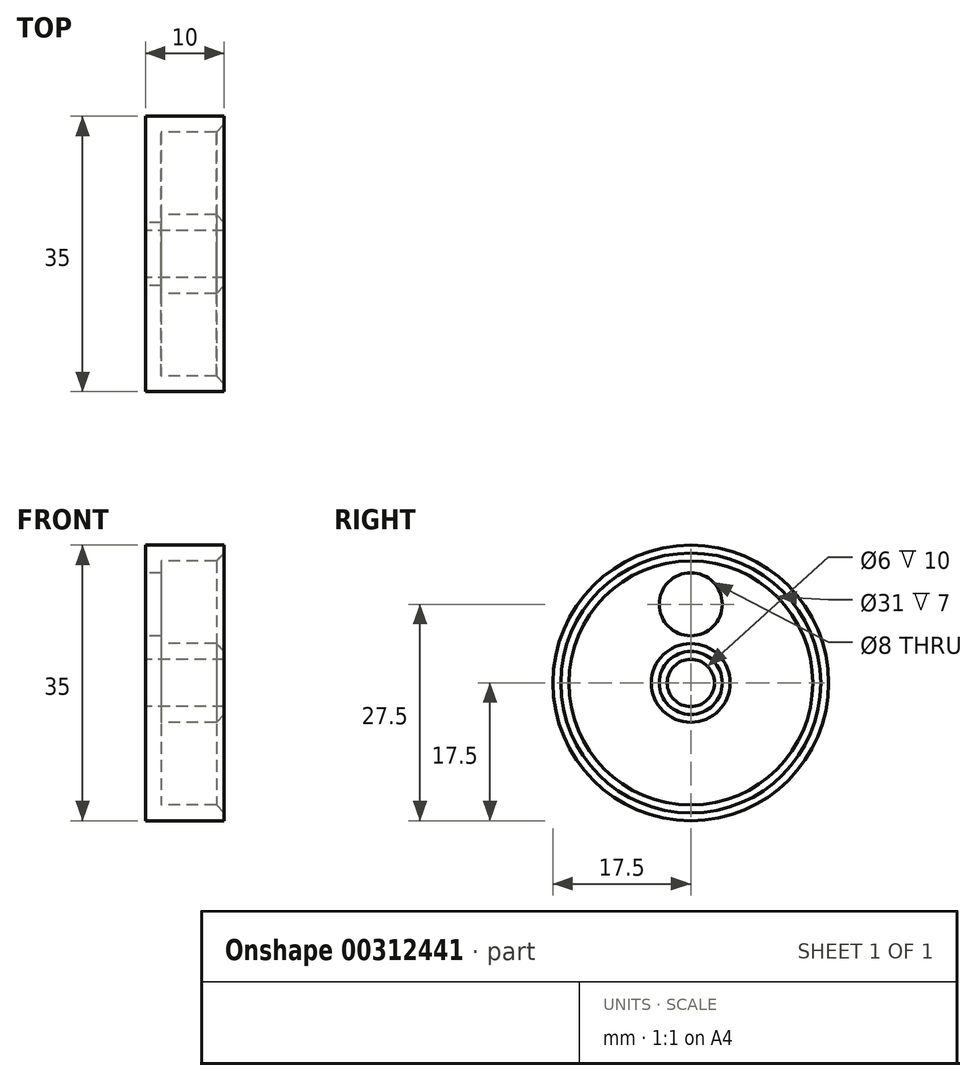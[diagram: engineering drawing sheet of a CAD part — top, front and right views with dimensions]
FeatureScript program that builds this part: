
annotation { "Feature Type Name" : "Feature", "Feature Type Description" : "" }
export const myFeature = defineFeature(function(context is Context, id is Id, definition is map)
    precondition{}
    {
        {
            var Q0;
            Q0=qCreatedBy(makeId("Front.planeOp"),FACE);
            var sketch = newSketch(context, id + "F0", { "sketchPlane" : qUnion([Q0])});
            skPoint(sketch, "E0", {"position": v(0, 0) * mm});
            skLineSegment(sketch, "E1.bottom", {"start": v(0, 0) * mm, "end": v(10, 0) * mm});
            skLineSegment(sketch, "E1.top", {"start": v(0, 17.5) * mm, "end": v(10, 17.5) * mm});
            skLineSegment(sketch, "E1.left", {"start": v(0, 0) * mm, "end": v(0, 17.5) * mm});
            skLineSegment(sketch, "E1.right", {"start": v(10, 0) * mm, "end": v(10, 17.5) * mm});
            skSolve(sketch);
        }
        {
            var Q0;
            Q0=makeQuery(id+"F0.imprint","IMPRINT",FACE,{"disambiguationData":[TD([[makeQuery(id+"F0.imprint","IMPRINT",EDGE,{"derivedFrom":sQuery(id+"F0.wireOp",EDGE,"E1.bottom")}),1.0]])]});
            var Q1;
            Q1=sQuery(id+"F0.wireOp",EDGE,"E1.bottom");
            revolve(context, id + "F1", {"entities" : qUnion([Q0]), "axis" : qUnion([Q1]), "revolveType" : RevolveType.FULL});
        }
        {
            var Q0;
            Q0=qCreatedBy(makeId("Right.planeOp"),FACE);
            var sketch = newSketch(context, id + "F2", { "sketchPlane" : qUnion([Q0])});
            skPoint(sketch, "E2", {"position": v(0, 0) * mm});
            skSolve(sketch);
        }
        {
            var Q0;
            Q0=sQuery(id+"F2.wireOp",VERTEX,"E2");
            var Q1;
            Q1=makeQuery(id+"F1.opRevolve","SWEPT_BODY",BODY,{"disambiguationData":[OSD([sQuery(id+"F0.wireOp",EDGE,"E1.bottom"),sQuery(id+"F0.wireOp",EDGE,"E1.top"),sQuery(id+"F0.wireOp",EDGE,"E1.left"),sQuery(id+"F0.wireOp",EDGE,"E1.right")])]});
            hole(context, id + "F3", {"style" : HoleStyle.SIMPLE, "endStyle" : HoleEndStyle.THROUGH, "oppositeDirection" : true, "holeDiameter" : 6 * mm, "tappedDepth" : 12 * mm, "tapClearance" : 3, "locations" : qUnion([Q0]), "scope" : qUnion([Q1])});
        }
        {
            var Q0;
            Q0=makeQuery(id+"F1.opRevolve","SWEPT_FACE",FACE,{"disambiguationData":[OSD([sQuery(id+"F0.wireOp",EDGE,"E1.right")])]});
            shell(context, id + "F4", {"entities" : qUnion([Q0]), "thickness" : 2 * mm});
        }
        {
            var Q0;
            Q0=makeQuery(id+"F1.opRevolve","SWEPT_FACE",FACE,{"disambiguationData":[OSD([sQuery(id+"F0.wireOp",EDGE,"E1.left")])]});
            var sketch = newSketch(context, id + "F5", { "sketchPlane" : qUnion([Q0])});
            skPoint(sketch, "E3", {"position": v(0, 10) * mm});
            skSolve(sketch);
        }
        {
            var Q0;
            Q0=sQuery(id+"F5.wireOp",VERTEX,"E3");
            var Q1;
            Q1=makeQuery(id+"F1.opRevolve","SWEPT_BODY",BODY,{"disambiguationData":[OSD([sQuery(id+"F0.wireOp",EDGE,"E1.bottom"),sQuery(id+"F0.wireOp",EDGE,"E1.top"),sQuery(id+"F0.wireOp",EDGE,"E1.left"),sQuery(id+"F0.wireOp",EDGE,"E1.right")])]});
            hole(context, id + "F6", {"style" : HoleStyle.SIMPLE, "endStyle" : HoleEndStyle.THROUGH, "holeDiameter" : 8 * mm, "tappedDepth" : 12 * mm, "tapClearance" : 3, "locations" : qUnion([Q0]), "scope" : qUnion([Q1])});
        }
        {
            var Q0;
            Q0=makeQuery(id+"F4.opShell","OFFSET_EDGE",EDGE,{"disambiguationData":[OSD([sQuery(id+"F0.wireOp",EDGE,"E1.right"),sQuery(id+"F3.hole-0.sketch.wireOp",EDGE,"core_line_2")])]});
            chamfer(context, id + "F7", {"entities" : qUnion([Q0]), "width" : 1 * mm, "tangentPropagation" : true});
        }
    });
